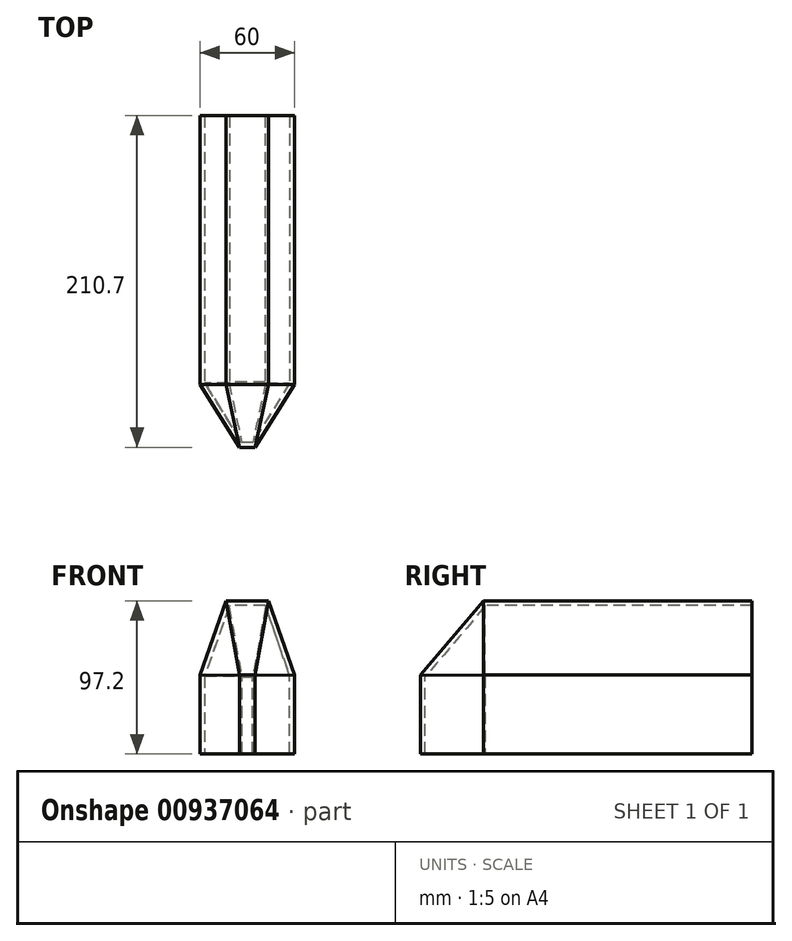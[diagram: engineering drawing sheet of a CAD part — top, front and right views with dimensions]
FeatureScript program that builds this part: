
annotation { "Feature Type Name" : "Feature", "Feature Type Description" : "" }
export const myFeature = defineFeature(function(context is Context, id is Id, definition is map)
    precondition{}
    {
        {
            var Q0;
            Q0=qCreatedBy(makeId("Front.planeOp"),FACE);
            var sketch = newSketch(context, id + "F0", { "sketchPlane" : qUnion([Q0])});
            skLineSegment(sketch, "E0", {"start": v(-30, 0) * mm, "end": v(30, 0) * mm});
            skLineSegment(sketch, "E1", {"start": v(30, 0) * mm, "end": v(30, 50) * mm});
            skLineSegment(sketch, "E2", {"start": v(30, 50) * mm, "end": v(13.5, 97.2) * mm});
            skLineSegment(sketch, "E3", {"start": v(13.5, 97.2) * mm, "end": v(-13.5, 97.2) * mm});
            skLineSegment(sketch, "E4", {"start": v(-13.5, 97.2) * mm, "end": v(-30, 50) * mm});
            skLineSegment(sketch, "E5", {"start": v(-30, 50) * mm, "end": v(-30, 0) * mm});
            skSolve(sketch);
        }
        {
            var Q0;
            Q0 = qSketchRegion(id + "F0", true);
            extrude(context, id + "F1", {"entities" : qUnion([Q0]), "oppositeDirection" : true, "depth" : 170.7 * mm, "offsetDistance" : 25 * mm});
        }
        {
            var Q0;
            Q0=makeQuery(id+"F1.opExtrude","CAP_FACE",FACE,{"disambiguationData":[OSD([sQuery(id+"F0.wireOp",EDGE,"E0"),sQuery(id+"F0.wireOp",EDGE,"E1"),sQuery(id+"F0.wireOp",EDGE,"E2"),sQuery(id+"F0.wireOp",EDGE,"E3"),sQuery(id+"F0.wireOp",EDGE,"E4"),sQuery(id+"F0.wireOp",EDGE,"E5")])],"isStart":true});
            cPlane(context, id + "F2", {"entities" : qUnion([Q0]), "cplaneType" : CPlaneType.OFFSET, "offset" : 40 * mm, "width" : 150 * mm, "height" : 150 * mm});
        }
        {
            var Q0;
            Q0=qCreatedBy(id+"F2.planeOp",FACE);
            var sketch = newSketch(context, id + "F3", { "sketchPlane" : qUnion([Q0])});
            skLineSegment(sketch, "E6.bottom", {"start": v(-5, 0) * mm, "end": v(5, 0) * mm});
            skLineSegment(sketch, "E6.top", {"start": v(-4.93, 50) * mm, "end": v(4.93, 50) * mm});
            skLineSegment(sketch, "E6.left", {"start": v(-5, 0) * mm, "end": v(-5, 49.93) * mm});
            skLineSegment(sketch, "E6.right", {"start": v(5, 0) * mm, "end": v(5, 49.93) * mm});
            skLineSegment(sketch, "E7", {"start": v(5, 49.93) * mm, "end": v(4.93, 50) * mm});
            skLineSegment(sketch, "E8", {"start": v(-5, 49.93) * mm, "end": v(-4.93, 50) * mm});
            skSolve(sketch);
        }
        {
            var Q1;
            Q1=makeQuery(id+"F3.imprint","IMPRINT",FACE,{"disambiguationData":[TD([[makeQuery(id+"F3.imprint","IMPRINT",EDGE,{"derivedFrom":sQuery(id+"F3.wireOp",EDGE,"E6.bottom")}),1.0]])]});
            var Q2;
            Q2=makeQuery(id+"F1.opExtrude","CAP_FACE",FACE,{"disambiguationData":[OSD([sQuery(id+"F0.wireOp",EDGE,"E0"),sQuery(id+"F0.wireOp",EDGE,"E1"),sQuery(id+"F0.wireOp",EDGE,"E2"),sQuery(id+"F0.wireOp",EDGE,"E3"),sQuery(id+"F0.wireOp",EDGE,"E4"),sQuery(id+"F0.wireOp",EDGE,"E5")])],"isStart":true});
            loft(context, id + "F4", {"operationType" : NewBodyOperationType.ADD, "sheetProfilesArray" : [{ "sheetProfileEntities" : qUnion([Q1]) }, { "sheetProfileEntities" : qUnion([Q2]) }]});
        }
        {
            var Q0;
            {var subQ0=sQuery(id+"F0.wireOp",EDGE,"E0");Q0=makeQuery(id+"F4.boolean.opBoolean","MERGE",FACE,{"derivedFrom":[makeQuery(id+"F1.opExtrude","SWEPT_FACE",FACE,{"disambiguationData":[OSD([subQ0])]}),makeQuery(id+"F4.opLoft","SWEPT_FACE",FACE,{"disambiguationData":[OSD([subQ0,sQuery(id+"F0.wireOp",EDGE,"E1"),sQuery(id+"F0.wireOp",EDGE,"E5"),sQuery(id+"F3.wireOp",EDGE,"E6.bottom"),sQuery(id+"F3.wireOp",EDGE,"E6.left"),sQuery(id+"F3.wireOp",EDGE,"E6.right")])]})]});}
            var Q1;
            Q1=makeQuery(id+"F1.opExtrude","CAP_FACE",FACE,{"disambiguationData":[OSD([sQuery(id+"F0.wireOp",EDGE,"E0"),sQuery(id+"F0.wireOp",EDGE,"E1"),sQuery(id+"F0.wireOp",EDGE,"E2"),sQuery(id+"F0.wireOp",EDGE,"E3"),sQuery(id+"F0.wireOp",EDGE,"E4"),sQuery(id+"F0.wireOp",EDGE,"E5")])],"isStart":false});
            shell(context, id + "F5", {"entities" : qUnion([Q0, Q1]), "thickness" : 3 * mm});
        }
    });
